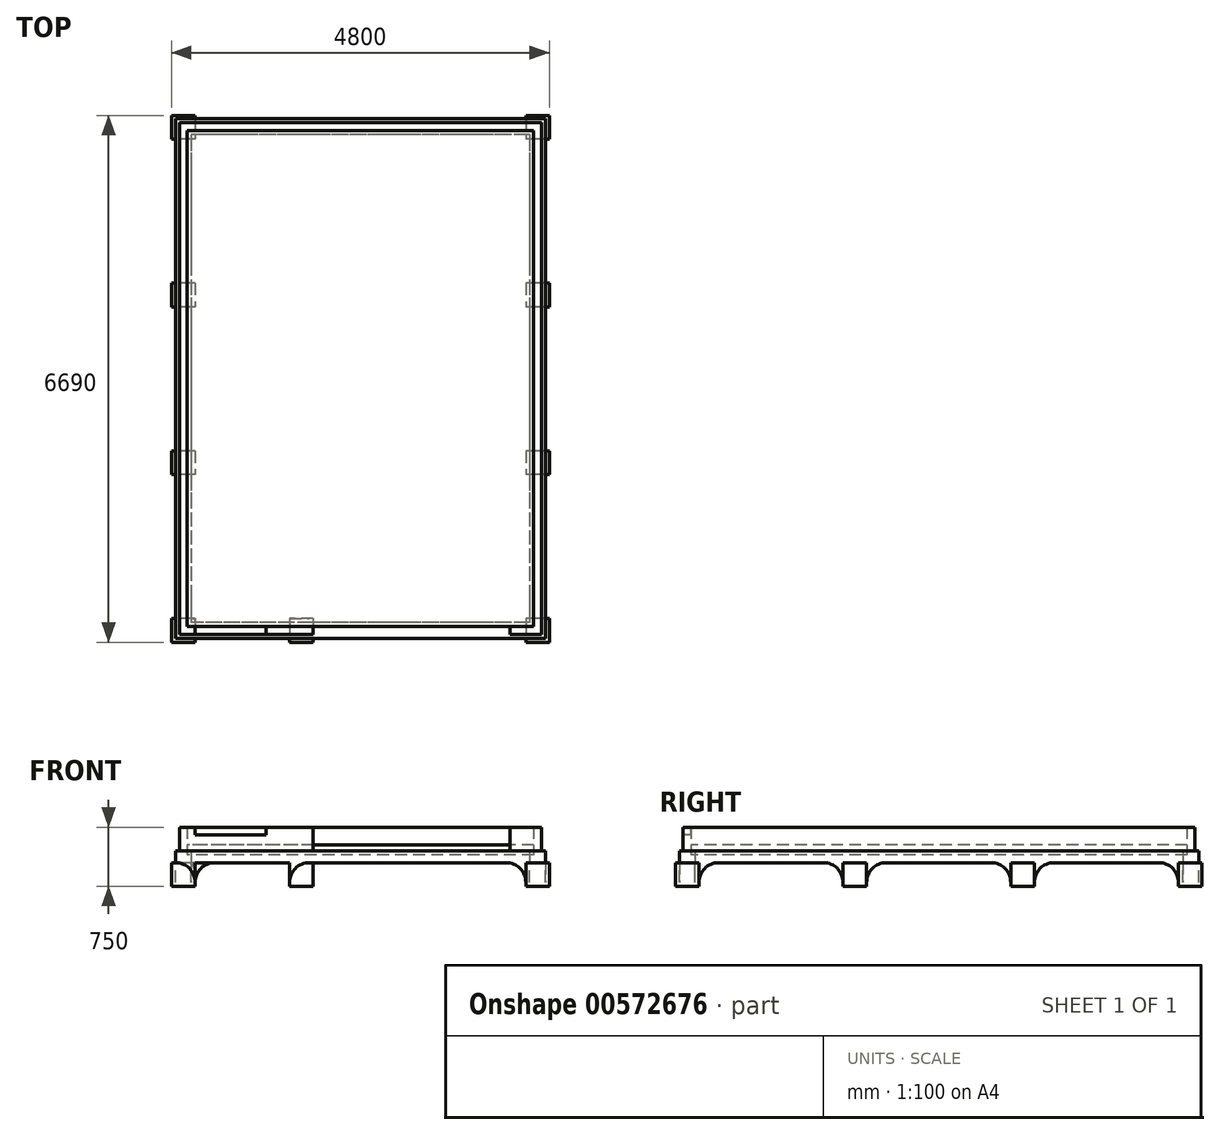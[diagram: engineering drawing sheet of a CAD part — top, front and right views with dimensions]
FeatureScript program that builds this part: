
annotation { "Feature Type Name" : "Feature", "Feature Type Description" : "" }
export const myFeature = defineFeature(function(context is Context, id is Id, definition is map)
    precondition{}
    {
        {
            var Q0;
            Q0=qCreatedBy(makeId("Top.planeOp"),FACE);
            var sketch = newSketch(context, id + "F0", { "sketchPlane" : qUnion([Q0])});
            skLineSegment(sketch, "E0.bottom", {"start": v(2350, 3300) * mm, "end": v(-2350, 3300) * mm});
            skLineSegment(sketch, "E0.top", {"start": v(2350, -3300) * mm, "end": v(-2350, -3300) * mm});
            skLineSegment(sketch, "E0.left", {"start": v(2350, 3300) * mm, "end": v(2350, -3300) * mm});
            skLineSegment(sketch, "E0.right", {"start": v(-2350, 3300) * mm, "end": v(-2350, -3300) * mm});
            skPoint(sketch, "E0.middle", {"position": v(0, 0) * mm});
            skLineSegment(sketch, "E1.0", {"start": v(2150, 3100) * mm, "end": v(2150, -3100) * mm});
            skLineSegment(sketch, "E1.1", {"start": v(2150, 3100) * mm, "end": v(-2150, 3100) * mm});
            skLineSegment(sketch, "E1.2", {"start": v(-2150, 3100) * mm, "end": v(-2150, -3100) * mm});
            skLineSegment(sketch, "E1.3", {"start": v(2150, -3100) * mm, "end": v(-2150, -3100) * mm});
            skSolve(sketch);
        }
        {
            var Q0;
            Q0=makeQuery(id+"F0.imprint","IMPRINT",FACE,{"disambiguationData":[TD([[makeQuery(id+"F0.imprint","IMPRINT",EDGE,{"derivedFrom":sQuery(id+"F0.wireOp",EDGE,"E0.bottom")}),1.0]])]});
            extrude(context, id + "F1", {"entities" : qUnion([Q0]), "depth" : 150 * mm, "offsetDistance" : 25 * mm});
        }
        {
            var Q0;
            Q0=makeQuery(id+"F1.opExtrude","CAP_FACE",FACE,{"disambiguationData":[OSD([sQuery(id+"F0.wireOp",EDGE,"E0.bottom"),sQuery(id+"F0.wireOp",EDGE,"E0.top"),sQuery(id+"F0.wireOp",EDGE,"E0.left"),sQuery(id+"F0.wireOp",EDGE,"E0.right"),sQuery(id+"F0.wireOp",EDGE,"E1.0"),sQuery(id+"F0.wireOp",EDGE,"E1.1"),sQuery(id+"F0.wireOp",EDGE,"E1.2"),sQuery(id+"F0.wireOp",EDGE,"E1.3")])],"isStart":false});
            var sketch = newSketch(context, id + "F2", { "sketchPlane" : qUnion([Q0])});
            skLineSegment(sketch, "E2.0", {"start": v(-2300, 3250) * mm, "end": v(-2300, -3250) * mm});
            skLineSegment(sketch, "E2.1", {"start": v(2300, 3250) * mm, "end": v(-2300, 3250) * mm});
            skLineSegment(sketch, "E2.2", {"start": v(2300, 3250) * mm, "end": v(2300, -3250) * mm});
            skLineSegment(sketch, "E2.3", {"start": v(2300, -3250) * mm, "end": v(-2300, -3250) * mm});
            skLineSegment(sketch, "E3.0", {"start": v(-2200, 3150) * mm, "end": v(-2200, -3150) * mm});
            skLineSegment(sketch, "E3.1", {"start": v(2200, 3150) * mm, "end": v(-2200, 3150) * mm});
            skLineSegment(sketch, "E3.2", {"start": v(2200, 3150) * mm, "end": v(2200, -3150) * mm});
            skLineSegment(sketch, "E3.3", {"start": v(2200, -3150) * mm, "end": v(-2200, -3150) * mm});
            skSolve(sketch);
        }
        {
            var Q0;
            Q0 = qSketchRegion(id + "F2", true);
            extrude(context, id + "F3", {"entities" : qUnion([Q0]), "operationType" : NewBodyOperationType.ADD, "depth" : 300 * mm, "offsetDistance" : 25 * mm});
        }
        {
            var Q0;
            Q0=qCreatedBy(makeId("Top.planeOp"),FACE);
            var sketch = newSketch(context, id + "F4", { "sketchPlane" : qUnion([Q0])});
            skLineSegment(sketch, "E4.bottom", {"start": v(-2100, -3050) * mm, "end": v(-2400, -3050) * mm});
            skLineSegment(sketch, "E4.top", {"start": v(-2100, -3350) * mm, "end": v(-2400, -3350) * mm});
            skLineSegment(sketch, "E4.left", {"start": v(-2100, -3050) * mm, "end": v(-2100, -3350) * mm});
            skLineSegment(sketch, "E4.right", {"start": v(-2400, -3050) * mm, "end": v(-2400, -3350) * mm});
            skLineSegment(sketch, "E5.0.1.0", {"start": v(-2400, -920) * mm, "end": v(-2400, -1220) * mm});
            skLineSegment(sketch, "E5.0.1.1", {"start": v(-2100, -920) * mm, "end": v(-2400, -920) * mm});
            skLineSegment(sketch, "E5.0.1.2", {"start": v(-2100, -1220) * mm, "end": v(-2400, -1220) * mm});
            skLineSegment(sketch, "E5.0.1.3", {"start": v(-2100, -920) * mm, "end": v(-2100, -1220) * mm});
            skLineSegment(sketch, "E5.1.0.0", {"start": v(2100, -3050) * mm, "end": v(2100, -3350) * mm});
            skLineSegment(sketch, "E5.1.0.1", {"start": v(2400, -3050) * mm, "end": v(2100, -3050) * mm});
            skLineSegment(sketch, "E5.1.0.2", {"start": v(2400, -3350) * mm, "end": v(2100, -3350) * mm});
            skLineSegment(sketch, "E5.1.0.3", {"start": v(2400, -3050) * mm, "end": v(2400, -3350) * mm});
            skLineSegment(sketch, "E5.1.1.0", {"start": v(2100, -920) * mm, "end": v(2100, -1220) * mm});
            skLineSegment(sketch, "E5.1.1.1", {"start": v(2400, -920) * mm, "end": v(2100, -920) * mm});
            skLineSegment(sketch, "E5.1.1.2", {"start": v(2400, -1220) * mm, "end": v(2100, -1220) * mm});
            skLineSegment(sketch, "E5.1.1.3", {"start": v(2400, -920) * mm, "end": v(2400, -1220) * mm});
            skLineSegment(sketch, "E5.direction1", {"start": v(-2400, -3350) * mm, "end": v(2100, -3350) * mm, "construction": true});
            skLineSegment(sketch, "E5.direction2", {"start": v(-2400, -3350) * mm, "end": v(-2400, -1220) * mm, "construction": true});
            skLineSegment(sketch, "E6.0.0.2", {"start": v(-2400, 1210) * mm, "end": v(-2400, 910) * mm});
            skLineSegment(sketch, "E6.3.0.2", {"start": v(-2100, 1210) * mm, "end": v(-2400, 1210) * mm});
            skLineSegment(sketch, "E6.6.0.2", {"start": v(-2100, 910) * mm, "end": v(-2400, 910) * mm});
            skLineSegment(sketch, "E6.9.0.2", {"start": v(-2100, 1210) * mm, "end": v(-2100, 910) * mm});
            skLineSegment(sketch, "E6.0.0.3", {"start": v(-2400, 3340) * mm, "end": v(-2400, 3040) * mm});
            skLineSegment(sketch, "E6.3.0.3", {"start": v(-2100, 3340) * mm, "end": v(-2400, 3340) * mm});
            skLineSegment(sketch, "E6.6.0.3", {"start": v(-2100, 3040) * mm, "end": v(-2400, 3040) * mm});
            skLineSegment(sketch, "E6.9.0.3", {"start": v(-2100, 3340) * mm, "end": v(-2100, 3040) * mm});
            skLineSegment(sketch, "E6.0.1.2", {"start": v(2100, 1210) * mm, "end": v(2100, 910) * mm});
            skLineSegment(sketch, "E6.3.1.2", {"start": v(2400, 1210) * mm, "end": v(2100, 1210) * mm});
            skLineSegment(sketch, "E6.6.1.2", {"start": v(2400, 910) * mm, "end": v(2100, 910) * mm});
            skLineSegment(sketch, "E6.9.1.2", {"start": v(2400, 1210) * mm, "end": v(2400, 910) * mm});
            skLineSegment(sketch, "E6.0.1.3", {"start": v(2100, 3340) * mm, "end": v(2100, 3040) * mm});
            skLineSegment(sketch, "E6.3.1.3", {"start": v(2400, 3340) * mm, "end": v(2100, 3340) * mm});
            skLineSegment(sketch, "E6.6.1.3", {"start": v(2400, 3040) * mm, "end": v(2100, 3040) * mm});
            skLineSegment(sketch, "E6.9.1.3", {"start": v(2400, 3340) * mm, "end": v(2400, 3040) * mm});
            skLineSegment(sketch, "E7.1.0.0", {"start": v(-900, -3050) * mm, "end": v(-900, -3350) * mm});
            skLineSegment(sketch, "E7.1.0.1", {"start": v(-600, -3050) * mm, "end": v(-900, -3050) * mm});
            skLineSegment(sketch, "E7.1.0.2", {"start": v(-600, -3350) * mm, "end": v(-900, -3350) * mm});
            skLineSegment(sketch, "E7.1.0.3", {"start": v(-600, -3050) * mm, "end": v(-600, -3350) * mm});
            skLineSegment(sketch, "E7.direction1", {"start": v(-2100, -3350) * mm, "end": v(-600, -3350) * mm, "construction": true});
            skSolve(sketch);
        }
        {
            var Q0;
            Q0 = qSketchRegion(id + "F4", true);
            extrude(context, id + "F5", {"entities" : qUnion([Q0]), "operationType" : NewBodyOperationType.ADD, "oppositeDirection" : true, "depth" : 300 * mm, "offsetDistance" : 25 * mm});
        }
        {
            var Q0;
            Q0=makeQuery(id+"F1.opExtrude","SWEPT_FACE",FACE,{"disambiguationData":[OSD([sQuery(id+"F0.wireOp",EDGE,"E0.top")])]});
            var sketch = newSketch(context, id + "F6", { "sketchPlane" : qUnion([Q0])});
            skLineSegment(sketch, "E8.bottom", {"start": v(-600, 650) * mm, "end": v(1900, 650) * mm});
            skLineSegment(sketch, "E8.top", {"start": v(-600, 150) * mm, "end": v(1900, 150) * mm});
            skLineSegment(sketch, "E8.left", {"start": v(-600, 650) * mm, "end": v(-600, 150) * mm});
            skLineSegment(sketch, "E8.right", {"start": v(1900, 650) * mm, "end": v(1900, 150) * mm});
            skSolve(sketch);
        }
        {
            var Q0;
            Q0 = qSketchRegion(id + "F6", true);
            var Q1;
            Q1=makeQuery(id+"F1.opExtrude","SWEPT_FACE",FACE,{"disambiguationData":[OSD([sQuery(id+"F0.wireOp",EDGE,"E1.3")])]});
            extrude(context, id + "F7", {"entities" : qUnion([Q0, Q1]), "operationType" : NewBodyOperationType.REMOVE, "oppositeDirection" : true, "depth" : 500 * mm, "offsetDistance" : 25 * mm});
        }
        {
            var Q0;
            Q0=qCreatedBy(makeId("Top.planeOp"),FACE);
            cPlane(context, id + "F8", {"entities" : qUnion([Q0]), "cplaneType" : CPlaneType.OFFSET, "offset" : 100 * mm, "width" : 150 * mm, "height" : 150 * mm});
        }
        {
            var Q0;
            Q0=qCreatedBy(id+"F8.planeOp",FACE);
            var sketch = newSketch(context, id + "F9", { "sketchPlane" : qUnion([Q0])});
            skLineSegment(sketch, "E9.bottom", {"start": v(2200, 3150) * mm, "end": v(-2200, 3150) * mm});
            skLineSegment(sketch, "E9.top", {"start": v(2200, -3150) * mm, "end": v(-2200, -3150) * mm});
            skLineSegment(sketch, "E9.left", {"start": v(2200, 3150) * mm, "end": v(2200, -3150) * mm});
            skLineSegment(sketch, "E9.right", {"start": v(-2200, 3150) * mm, "end": v(-2200, -3150) * mm});
            skPoint(sketch, "E9.middle", {"position": v(0, 0) * mm});
            skSolve(sketch);
        }
        {
            var Q0;
            Q0=makeQuery(id+"F9.imprint","IMPRINT",FACE,{"disambiguationData":[TD([[makeQuery(id+"F9.imprint","IMPRINT",EDGE,{"derivedFrom":sQuery(id+"F9.wireOp",EDGE,"E9.bottom")}),1.0]])]});
            extrude(context, id + "F10", {"entities" : qUnion([Q0]), "depth" : 125 * mm, "offsetDistance" : 25 * mm});
        }
        {
            var Q0;
            {var subQ0=sQuery(id+"F4.wireOp",EDGE,"E6.9.0.3");Q0=makeQuery(id+"F5.boolean.opBoolean","SPLIT",EDGE,{"disambiguationData":[topologyDisambiguationEdgeConnected([makeQuery(id+"F1.opExtrude","CAP_FACE",FACE,{"disambiguationData":[OSD([sQuery(id+"F0.wireOp",EDGE,"E0.bottom"),sQuery(id+"F0.wireOp",EDGE,"E0.top"),sQuery(id+"F0.wireOp",EDGE,"E0.left"),sQuery(id+"F0.wireOp",EDGE,"E0.right"),sQuery(id+"F0.wireOp",EDGE,"E1.0"),sQuery(id+"F0.wireOp",EDGE,"E1.1"),sQuery(id+"F0.wireOp",EDGE,"E1.2"),sQuery(id+"F0.wireOp",EDGE,"E1.3")])],"isStart":true}),makeQuery(id+"F5.opExtrude","SWEPT_FACE",FACE,{"disambiguationData":[OSD([subQ0])]})])],"derivedFrom":makeQuery(id+"F5.opExtrude","CAP_EDGE",EDGE,{"disambiguationData":[OSD([subQ0])],"isStart":true})});}
            var Q1;
            {var subQ0=sQuery(id+"F4.wireOp",EDGE,"E6.6.0.3");Q1=makeQuery(id+"F5.boolean.opBoolean","SPLIT",EDGE,{"disambiguationData":[topologyDisambiguationEdgeConnected([makeQuery(id+"F1.opExtrude","CAP_FACE",FACE,{"disambiguationData":[OSD([sQuery(id+"F0.wireOp",EDGE,"E0.bottom"),sQuery(id+"F0.wireOp",EDGE,"E0.top"),sQuery(id+"F0.wireOp",EDGE,"E0.left"),sQuery(id+"F0.wireOp",EDGE,"E0.right"),sQuery(id+"F0.wireOp",EDGE,"E1.0"),sQuery(id+"F0.wireOp",EDGE,"E1.1"),sQuery(id+"F0.wireOp",EDGE,"E1.2"),sQuery(id+"F0.wireOp",EDGE,"E1.3")])],"isStart":true}),makeQuery(id+"F5.opExtrude","SWEPT_FACE",FACE,{"disambiguationData":[OSD([subQ0])]})])],"derivedFrom":makeQuery(id+"F5.opExtrude","CAP_EDGE",EDGE,{"disambiguationData":[OSD([subQ0])],"isStart":true})});}
            var Q2;
            {var subQ0=sQuery(id+"F4.wireOp",EDGE,"E6.3.0.2");Q2=makeQuery(id+"F5.boolean.opBoolean","SPLIT",EDGE,{"disambiguationData":[topologyDisambiguationEdgeConnected([makeQuery(id+"F1.opExtrude","CAP_FACE",FACE,{"disambiguationData":[OSD([sQuery(id+"F0.wireOp",EDGE,"E0.bottom"),sQuery(id+"F0.wireOp",EDGE,"E0.top"),sQuery(id+"F0.wireOp",EDGE,"E0.left"),sQuery(id+"F0.wireOp",EDGE,"E0.right"),sQuery(id+"F0.wireOp",EDGE,"E1.0"),sQuery(id+"F0.wireOp",EDGE,"E1.1"),sQuery(id+"F0.wireOp",EDGE,"E1.2"),sQuery(id+"F0.wireOp",EDGE,"E1.3")])],"isStart":true}),makeQuery(id+"F5.opExtrude","SWEPT_FACE",FACE,{"disambiguationData":[OSD([subQ0])]})])],"derivedFrom":makeQuery(id+"F5.opExtrude","CAP_EDGE",EDGE,{"disambiguationData":[OSD([subQ0])],"isStart":true})});}
            var Q3;
            {var subQ0=sQuery(id+"F4.wireOp",EDGE,"E6.6.0.2");Q3=makeQuery(id+"F5.boolean.opBoolean","SPLIT",EDGE,{"disambiguationData":[topologyDisambiguationEdgeConnected([makeQuery(id+"F1.opExtrude","CAP_FACE",FACE,{"disambiguationData":[OSD([sQuery(id+"F0.wireOp",EDGE,"E0.bottom"),sQuery(id+"F0.wireOp",EDGE,"E0.top"),sQuery(id+"F0.wireOp",EDGE,"E0.left"),sQuery(id+"F0.wireOp",EDGE,"E0.right"),sQuery(id+"F0.wireOp",EDGE,"E1.0"),sQuery(id+"F0.wireOp",EDGE,"E1.1"),sQuery(id+"F0.wireOp",EDGE,"E1.2"),sQuery(id+"F0.wireOp",EDGE,"E1.3")])],"isStart":true}),makeQuery(id+"F5.opExtrude","SWEPT_FACE",FACE,{"disambiguationData":[OSD([subQ0])]})])],"derivedFrom":makeQuery(id+"F5.opExtrude","CAP_EDGE",EDGE,{"disambiguationData":[OSD([subQ0])],"isStart":true})});}
            var Q4;
            {var subQ0=sQuery(id+"F4.wireOp",EDGE,"E5.0.1.2");Q4=makeQuery(id+"F5.boolean.opBoolean","SPLIT",EDGE,{"disambiguationData":[topologyDisambiguationEdgeConnected([makeQuery(id+"F1.opExtrude","CAP_FACE",FACE,{"disambiguationData":[OSD([sQuery(id+"F0.wireOp",EDGE,"E0.bottom"),sQuery(id+"F0.wireOp",EDGE,"E0.top"),sQuery(id+"F0.wireOp",EDGE,"E0.left"),sQuery(id+"F0.wireOp",EDGE,"E0.right"),sQuery(id+"F0.wireOp",EDGE,"E1.0"),sQuery(id+"F0.wireOp",EDGE,"E1.1"),sQuery(id+"F0.wireOp",EDGE,"E1.2"),sQuery(id+"F0.wireOp",EDGE,"E1.3")])],"isStart":true}),makeQuery(id+"F5.opExtrude","SWEPT_FACE",FACE,{"disambiguationData":[OSD([subQ0])]})])],"derivedFrom":makeQuery(id+"F5.opExtrude","CAP_EDGE",EDGE,{"disambiguationData":[OSD([subQ0])],"isStart":true})});}
            var Q5;
            {var subQ0=sQuery(id+"F4.wireOp",EDGE,"E5.0.1.1");Q5=makeQuery(id+"F5.boolean.opBoolean","SPLIT",EDGE,{"disambiguationData":[topologyDisambiguationEdgeConnected([makeQuery(id+"F1.opExtrude","CAP_FACE",FACE,{"disambiguationData":[OSD([sQuery(id+"F0.wireOp",EDGE,"E0.bottom"),sQuery(id+"F0.wireOp",EDGE,"E0.top"),sQuery(id+"F0.wireOp",EDGE,"E0.left"),sQuery(id+"F0.wireOp",EDGE,"E0.right"),sQuery(id+"F0.wireOp",EDGE,"E1.0"),sQuery(id+"F0.wireOp",EDGE,"E1.1"),sQuery(id+"F0.wireOp",EDGE,"E1.2"),sQuery(id+"F0.wireOp",EDGE,"E1.3")])],"isStart":true}),makeQuery(id+"F5.opExtrude","SWEPT_FACE",FACE,{"disambiguationData":[OSD([subQ0])]})])],"derivedFrom":makeQuery(id+"F5.opExtrude","CAP_EDGE",EDGE,{"disambiguationData":[OSD([subQ0])],"isStart":true})});}
            var Q6;
            {var subQ0=sQuery(id+"F4.wireOp",EDGE,"E4.bottom");Q6=makeQuery(id+"F5.boolean.opBoolean","SPLIT",EDGE,{"disambiguationData":[topologyDisambiguationEdgeConnected([makeQuery(id+"F1.opExtrude","CAP_FACE",FACE,{"disambiguationData":[OSD([sQuery(id+"F0.wireOp",EDGE,"E0.bottom"),sQuery(id+"F0.wireOp",EDGE,"E0.top"),sQuery(id+"F0.wireOp",EDGE,"E0.left"),sQuery(id+"F0.wireOp",EDGE,"E0.right"),sQuery(id+"F0.wireOp",EDGE,"E1.0"),sQuery(id+"F0.wireOp",EDGE,"E1.1"),sQuery(id+"F0.wireOp",EDGE,"E1.2"),sQuery(id+"F0.wireOp",EDGE,"E1.3")])],"isStart":true}),makeQuery(id+"F5.opExtrude","SWEPT_FACE",FACE,{"disambiguationData":[OSD([subQ0])]})])],"derivedFrom":makeQuery(id+"F5.opExtrude","CAP_EDGE",EDGE,{"disambiguationData":[OSD([subQ0])],"isStart":true})});}
            var Q7;
            {var subQ0=sQuery(id+"F4.wireOp",EDGE,"E7.1.0.0");Q7=makeQuery(id+"F5.boolean.opBoolean","SPLIT",EDGE,{"disambiguationData":[topologyDisambiguationEdgeConnected([makeQuery(id+"F1.opExtrude","CAP_FACE",FACE,{"disambiguationData":[OSD([sQuery(id+"F0.wireOp",EDGE,"E0.bottom"),sQuery(id+"F0.wireOp",EDGE,"E0.top"),sQuery(id+"F0.wireOp",EDGE,"E0.left"),sQuery(id+"F0.wireOp",EDGE,"E0.right"),sQuery(id+"F0.wireOp",EDGE,"E1.0"),sQuery(id+"F0.wireOp",EDGE,"E1.1"),sQuery(id+"F0.wireOp",EDGE,"E1.2"),sQuery(id+"F0.wireOp",EDGE,"E1.3")])],"isStart":true}),makeQuery(id+"F5.opExtrude","SWEPT_FACE",FACE,{"disambiguationData":[OSD([subQ0])]})])],"derivedFrom":makeQuery(id+"F5.opExtrude","CAP_EDGE",EDGE,{"disambiguationData":[OSD([subQ0])],"isStart":true})});}
            var Q8;
            {var subQ0=sQuery(id+"F4.wireOp",EDGE,"E4.left");Q8=makeQuery(id+"F5.boolean.opBoolean","SPLIT",EDGE,{"disambiguationData":[topologyDisambiguationEdgeConnected([makeQuery(id+"F1.opExtrude","CAP_FACE",FACE,{"disambiguationData":[OSD([sQuery(id+"F0.wireOp",EDGE,"E0.bottom"),sQuery(id+"F0.wireOp",EDGE,"E0.top"),sQuery(id+"F0.wireOp",EDGE,"E0.left"),sQuery(id+"F0.wireOp",EDGE,"E0.right"),sQuery(id+"F0.wireOp",EDGE,"E1.0"),sQuery(id+"F0.wireOp",EDGE,"E1.1"),sQuery(id+"F0.wireOp",EDGE,"E1.2"),sQuery(id+"F0.wireOp",EDGE,"E1.3")])],"isStart":true}),makeQuery(id+"F5.opExtrude","SWEPT_FACE",FACE,{"disambiguationData":[OSD([subQ0])]})])],"derivedFrom":makeQuery(id+"F5.opExtrude","CAP_EDGE",EDGE,{"disambiguationData":[OSD([subQ0])],"isStart":true})});}
            var Q9;
            {var subQ0=sQuery(id+"F4.wireOp",EDGE,"E5.1.0.0");Q9=makeQuery(id+"F5.boolean.opBoolean","SPLIT",EDGE,{"disambiguationData":[topologyDisambiguationEdgeConnected([makeQuery(id+"F1.opExtrude","CAP_FACE",FACE,{"disambiguationData":[OSD([sQuery(id+"F0.wireOp",EDGE,"E0.bottom"),sQuery(id+"F0.wireOp",EDGE,"E0.top"),sQuery(id+"F0.wireOp",EDGE,"E0.left"),sQuery(id+"F0.wireOp",EDGE,"E0.right"),sQuery(id+"F0.wireOp",EDGE,"E1.0"),sQuery(id+"F0.wireOp",EDGE,"E1.1"),sQuery(id+"F0.wireOp",EDGE,"E1.2"),sQuery(id+"F0.wireOp",EDGE,"E1.3")])],"isStart":true}),makeQuery(id+"F5.opExtrude","SWEPT_FACE",FACE,{"disambiguationData":[OSD([subQ0])]})])],"derivedFrom":makeQuery(id+"F5.opExtrude","CAP_EDGE",EDGE,{"disambiguationData":[OSD([subQ0])],"isStart":true})});}
            var Q10;
            {var subQ0=sQuery(id+"F4.wireOp",EDGE,"E5.1.1.2");Q10=makeQuery(id+"F5.boolean.opBoolean","SPLIT",EDGE,{"disambiguationData":[topologyDisambiguationEdgeConnected([makeQuery(id+"F1.opExtrude","CAP_FACE",FACE,{"disambiguationData":[OSD([sQuery(id+"F0.wireOp",EDGE,"E0.bottom"),sQuery(id+"F0.wireOp",EDGE,"E0.top"),sQuery(id+"F0.wireOp",EDGE,"E0.left"),sQuery(id+"F0.wireOp",EDGE,"E0.right"),sQuery(id+"F0.wireOp",EDGE,"E1.0"),sQuery(id+"F0.wireOp",EDGE,"E1.1"),sQuery(id+"F0.wireOp",EDGE,"E1.2"),sQuery(id+"F0.wireOp",EDGE,"E1.3")])],"isStart":true}),makeQuery(id+"F5.opExtrude","SWEPT_FACE",FACE,{"disambiguationData":[OSD([subQ0])]})])],"derivedFrom":makeQuery(id+"F5.opExtrude","CAP_EDGE",EDGE,{"disambiguationData":[OSD([subQ0])],"isStart":true})});}
            var Q11;
            {var subQ0=sQuery(id+"F4.wireOp",EDGE,"E6.6.1.2");Q11=makeQuery(id+"F5.boolean.opBoolean","SPLIT",EDGE,{"disambiguationData":[topologyDisambiguationEdgeConnected([makeQuery(id+"F1.opExtrude","CAP_FACE",FACE,{"disambiguationData":[OSD([sQuery(id+"F0.wireOp",EDGE,"E0.bottom"),sQuery(id+"F0.wireOp",EDGE,"E0.top"),sQuery(id+"F0.wireOp",EDGE,"E0.left"),sQuery(id+"F0.wireOp",EDGE,"E0.right"),sQuery(id+"F0.wireOp",EDGE,"E1.0"),sQuery(id+"F0.wireOp",EDGE,"E1.1"),sQuery(id+"F0.wireOp",EDGE,"E1.2"),sQuery(id+"F0.wireOp",EDGE,"E1.3")])],"isStart":true}),makeQuery(id+"F5.opExtrude","SWEPT_FACE",FACE,{"disambiguationData":[OSD([subQ0])]})])],"derivedFrom":makeQuery(id+"F5.opExtrude","CAP_EDGE",EDGE,{"disambiguationData":[OSD([subQ0])],"isStart":true})});}
            var Q12;
            {var subQ0=sQuery(id+"F4.wireOp",EDGE,"E6.6.1.3");Q12=makeQuery(id+"F5.boolean.opBoolean","SPLIT",EDGE,{"disambiguationData":[topologyDisambiguationEdgeConnected([makeQuery(id+"F1.opExtrude","CAP_FACE",FACE,{"disambiguationData":[OSD([sQuery(id+"F0.wireOp",EDGE,"E0.bottom"),sQuery(id+"F0.wireOp",EDGE,"E0.top"),sQuery(id+"F0.wireOp",EDGE,"E0.left"),sQuery(id+"F0.wireOp",EDGE,"E0.right"),sQuery(id+"F0.wireOp",EDGE,"E1.0"),sQuery(id+"F0.wireOp",EDGE,"E1.1"),sQuery(id+"F0.wireOp",EDGE,"E1.2"),sQuery(id+"F0.wireOp",EDGE,"E1.3")])],"isStart":true}),makeQuery(id+"F5.opExtrude","SWEPT_FACE",FACE,{"disambiguationData":[OSD([subQ0])]})])],"derivedFrom":makeQuery(id+"F5.opExtrude","CAP_EDGE",EDGE,{"disambiguationData":[OSD([subQ0])],"isStart":true})});}
            var Q13;
            {var subQ0=sQuery(id+"F4.wireOp",EDGE,"E6.0.1.3");Q13=makeQuery(id+"F5.boolean.opBoolean","SPLIT",EDGE,{"disambiguationData":[topologyDisambiguationEdgeConnected([makeQuery(id+"F1.opExtrude","CAP_FACE",FACE,{"disambiguationData":[OSD([sQuery(id+"F0.wireOp",EDGE,"E0.bottom"),sQuery(id+"F0.wireOp",EDGE,"E0.top"),sQuery(id+"F0.wireOp",EDGE,"E0.left"),sQuery(id+"F0.wireOp",EDGE,"E0.right"),sQuery(id+"F0.wireOp",EDGE,"E1.0"),sQuery(id+"F0.wireOp",EDGE,"E1.1"),sQuery(id+"F0.wireOp",EDGE,"E1.2"),sQuery(id+"F0.wireOp",EDGE,"E1.3")])],"isStart":true}),makeQuery(id+"F5.opExtrude","SWEPT_FACE",FACE,{"disambiguationData":[OSD([subQ0])]})])],"derivedFrom":makeQuery(id+"F5.opExtrude","CAP_EDGE",EDGE,{"disambiguationData":[OSD([subQ0])],"isStart":true})});}
            var Q14;
            {var subQ0=sQuery(id+"F4.wireOp",EDGE,"E5.1.0.1");Q14=makeQuery(id+"F5.boolean.opBoolean","SPLIT",EDGE,{"disambiguationData":[topologyDisambiguationEdgeConnected([makeQuery(id+"F1.opExtrude","CAP_FACE",FACE,{"disambiguationData":[OSD([sQuery(id+"F0.wireOp",EDGE,"E0.bottom"),sQuery(id+"F0.wireOp",EDGE,"E0.top"),sQuery(id+"F0.wireOp",EDGE,"E0.left"),sQuery(id+"F0.wireOp",EDGE,"E0.right"),sQuery(id+"F0.wireOp",EDGE,"E1.0"),sQuery(id+"F0.wireOp",EDGE,"E1.1"),sQuery(id+"F0.wireOp",EDGE,"E1.2"),sQuery(id+"F0.wireOp",EDGE,"E1.3")])],"isStart":true}),makeQuery(id+"F5.opExtrude","SWEPT_FACE",FACE,{"disambiguationData":[OSD([subQ0])]})])],"derivedFrom":makeQuery(id+"F5.opExtrude","CAP_EDGE",EDGE,{"disambiguationData":[OSD([subQ0])],"isStart":true})});}
            var Q15;
            {var subQ0=sQuery(id+"F4.wireOp",EDGE,"E5.1.1.1");Q15=makeQuery(id+"F5.boolean.opBoolean","SPLIT",EDGE,{"disambiguationData":[topologyDisambiguationEdgeConnected([makeQuery(id+"F1.opExtrude","CAP_FACE",FACE,{"disambiguationData":[OSD([sQuery(id+"F0.wireOp",EDGE,"E0.bottom"),sQuery(id+"F0.wireOp",EDGE,"E0.top"),sQuery(id+"F0.wireOp",EDGE,"E0.left"),sQuery(id+"F0.wireOp",EDGE,"E0.right"),sQuery(id+"F0.wireOp",EDGE,"E1.0"),sQuery(id+"F0.wireOp",EDGE,"E1.1"),sQuery(id+"F0.wireOp",EDGE,"E1.2"),sQuery(id+"F0.wireOp",EDGE,"E1.3")])],"isStart":true}),makeQuery(id+"F5.opExtrude","SWEPT_FACE",FACE,{"disambiguationData":[OSD([subQ0])]})])],"derivedFrom":makeQuery(id+"F5.opExtrude","CAP_EDGE",EDGE,{"disambiguationData":[OSD([subQ0])],"isStart":true})});}
            var Q16;
            {var subQ0=sQuery(id+"F4.wireOp",EDGE,"E6.3.1.2");Q16=makeQuery(id+"F5.boolean.opBoolean","SPLIT",EDGE,{"disambiguationData":[topologyDisambiguationEdgeConnected([makeQuery(id+"F1.opExtrude","CAP_FACE",FACE,{"disambiguationData":[OSD([sQuery(id+"F0.wireOp",EDGE,"E0.bottom"),sQuery(id+"F0.wireOp",EDGE,"E0.top"),sQuery(id+"F0.wireOp",EDGE,"E0.left"),sQuery(id+"F0.wireOp",EDGE,"E0.right"),sQuery(id+"F0.wireOp",EDGE,"E1.0"),sQuery(id+"F0.wireOp",EDGE,"E1.1"),sQuery(id+"F0.wireOp",EDGE,"E1.2"),sQuery(id+"F0.wireOp",EDGE,"E1.3")])],"isStart":true}),makeQuery(id+"F5.opExtrude","SWEPT_FACE",FACE,{"disambiguationData":[OSD([subQ0])]})])],"derivedFrom":makeQuery(id+"F5.opExtrude","CAP_EDGE",EDGE,{"disambiguationData":[OSD([subQ0])],"isStart":true})});}
            fillet(context, id + "F11", {"entities" : qUnion([Q0, Q1, Q2, Q3, Q4, Q5, Q6, Q7, Q8, Q9, Q10, Q11, Q12, Q13, Q14, Q15, Q16]), "radius" : 250 * mm, "tangentPropagation" : true, "allowEdgeOverflow" : false});
        }
        {
            var Q0;
            {var subQ0=sQuery(id+"F2.wireOp",EDGE,"E2.3");var subQ1=sQuery(id+"F2.wireOp",EDGE,"E2.0");Q0=makeQuery(id+"F7.boolean.opBoolean","SPLIT",FACE,{"disambiguationData":[TD([makeQuery(id+"F3.opExtrude","SWEPT_FACE",FACE,{"disambiguationData":[OSD([subQ1])]})])],"derivedFrom":makeQuery(id+"F3.opExtrude","SWEPT_FACE",FACE,{"disambiguationData":[OSD([subQ0])]})});}
            var sketch = newSketch(context, id + "F12", { "sketchPlane" : qUnion([Q0])});
            skLineSegment(sketch, "E10.bottom", {"start": v(-2100, 450) * mm, "end": v(-1200, 450) * mm});
            skLineSegment(sketch, "E10.top", {"start": v(-2100, 350) * mm, "end": v(-1200, 350) * mm});
            skLineSegment(sketch, "E10.left", {"start": v(-2100, 450) * mm, "end": v(-2100, 350) * mm});
            skLineSegment(sketch, "E10.right", {"start": v(-1200, 450) * mm, "end": v(-1200, 350) * mm});
            skSolve(sketch);
        }
        {
            var Q0;
            Q0 = qSketchRegion(id + "F12", true);
            var Q1;
            {var subQ0=sQuery(id+"F2.wireOp",EDGE,"E3.0");var subQ1=sQuery(id+"F2.wireOp",EDGE,"E3.3");Q1=makeQuery(id+"F7.boolean.opBoolean","SPLIT",FACE,{"disambiguationData":[TD([makeQuery(id+"F3.opExtrude","SWEPT_FACE",FACE,{"disambiguationData":[OSD([subQ0])]})])],"derivedFrom":makeQuery(id+"F3.opExtrude","SWEPT_FACE",FACE,{"disambiguationData":[OSD([subQ1])]})});}
            extrude(context, id + "F13", {"entities" : qUnion([Q0]), "operationType" : NewBodyOperationType.REMOVE, "endBound" : BoundingType.UP_TO_SURFACE, "oppositeDirection" : true, "depth" : 25 * mm, "endBoundEntityFace" : qUnion([Q1]), "offsetDistance" : 25 * mm});
        }
    });
